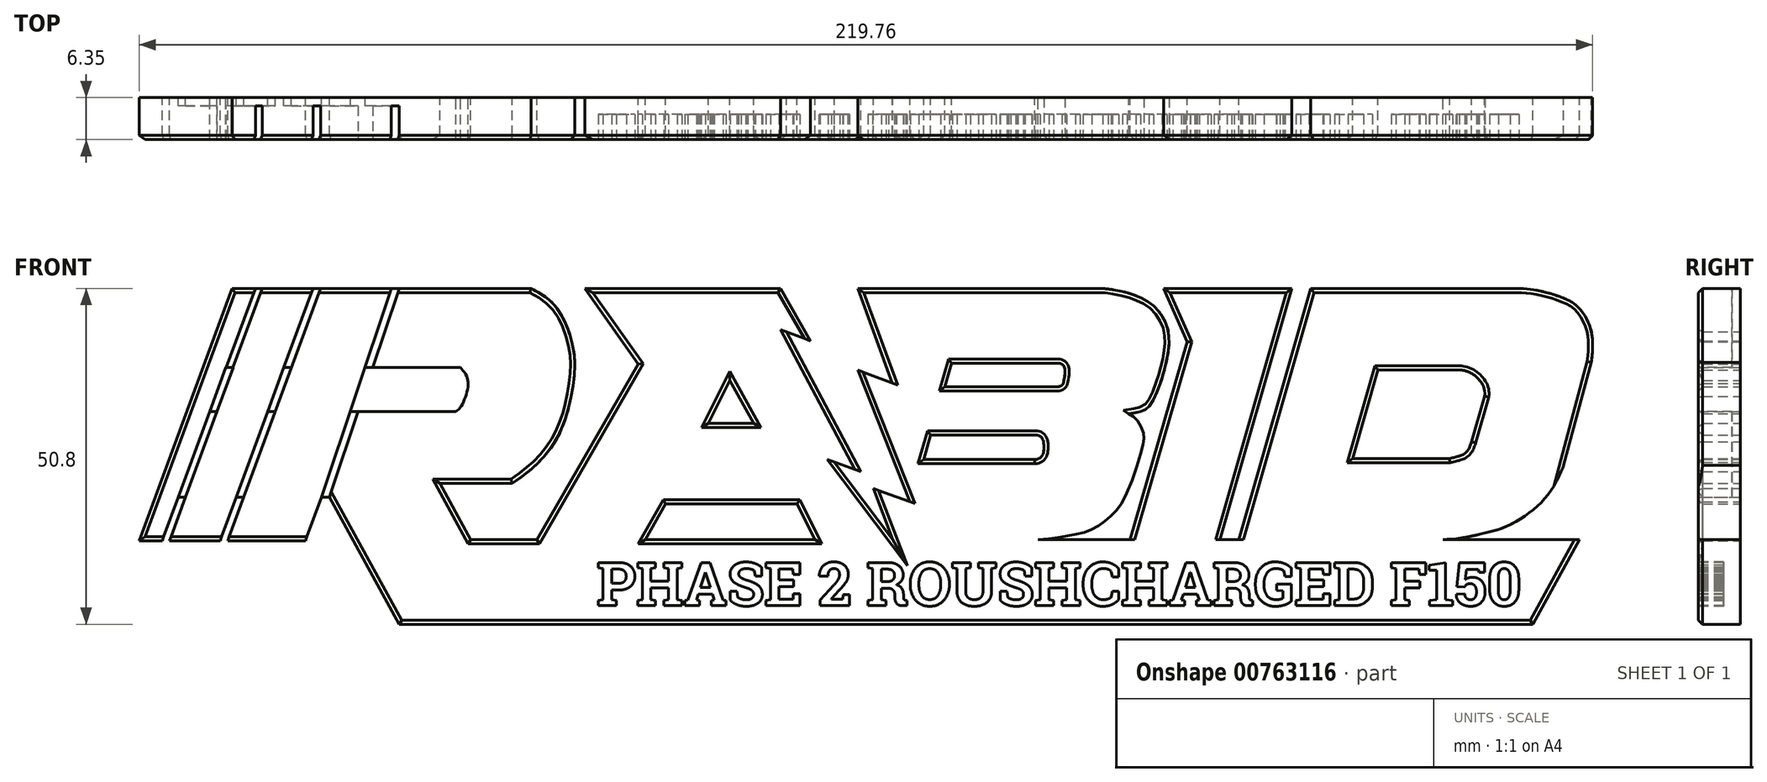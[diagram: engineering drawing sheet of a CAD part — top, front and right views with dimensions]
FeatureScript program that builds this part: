
annotation { "Feature Type Name" : "Feature", "Feature Type Description" : "" }
export const myFeature = defineFeature(function(context is Context, id is Id, definition is map)
    precondition{}
    {
        {
            var Q0;
            Q0=qCreatedBy(makeId("Front.planeOp"),FACE);
            var sketch = newSketch(context, id + "F0", { "sketchPlane" : qUnion([Q0])});
            skLineSegment(sketch, "E0", {"start": v(44.45, 18.23) * mm, "end": v(13.33, 18.23) * mm});
            skLineSegment(sketch, "E1", {"start": v(-163.82, -19.93) * mm, "end": v(-149.78, 18.23) * mm});
            skLineSegment(sketch, "E2", {"start": v(-138.67, -19.93) * mm, "end": v(-150.42, -19.93) * mm});
            skLineSegment(sketch, "E3", {"start": v(-146.28, 18.23) * mm, "end": v(-160.32, -19.93) * mm});
            skLineSegment(sketch, "E4", {"start": v(-159.23, -19.93) * mm, "end": v(-145.19, 18.23) * mm});
            skLineSegment(sketch, "E5", {"start": v(-137.53, 18.23) * mm, "end": v(-151.57, -19.93) * mm});
            skLineSegment(sketch, "E6", {"start": v(-150.42, -19.93) * mm, "end": v(-136.37, 18.23) * mm});
            skLineSegment(sketch, "E7", {"start": v(-124.63, 18.23) * mm, "end": v(-138.67, -19.93) * mm});
            skLineSegment(sketch, "E8", {"start": v(-127.97, 6.26) * mm, "end": v(-123.56, 18.23) * mm});
            skLineSegment(sketch, "E9", {"start": v(-127.97, 6.26) * mm, "end": v(-115.24, 6.26) * mm});
            skLineSegment(sketch, "E10", {"start": v(-115.92, -0.4) * mm, "end": v(-130.28, -0.4) * mm});
            skLineSegment(sketch, "E11", {"start": v(-130.28, -0.4) * mm, "end": v(-135.05, -13.36) * mm});
            skLineSegment(sketch, "E12", {"start": v(-135.05, -13.36) * mm, "end": v(-124.47, -32.57) * mm});
            skLineSegment(sketch, "E13", {"start": v(-124.47, -32.57) * mm, "end": v(-110.55, -32.57) * mm});
            skLineSegment(sketch, "E14", {"start": v(-110.55, -32.57) * mm, "end": v(-103.65, -19.74) * mm});
            skLineSegment(sketch, "E15", {"start": v(-103.65, -19.74) * mm, "end": v(-113.7, -19.74) * mm});
            skLineSegment(sketch, "E16", {"start": v(-113.7, -19.74) * mm, "end": v(-118.36, -11.28) * mm});
            skLineSegment(sketch, "E17", {"start": v(-118.36, -11.28) * mm, "end": v(-107.38, -11.28) * mm});
            skLineSegment(sketch, "E18", {"start": v(-103.65, -19.74) * mm, "end": v(-87.29, -19.74) * mm});
            skLineSegment(sketch, "E19", {"start": v(-96.42, 18.23) * mm, "end": v(-88.35, 6.81) * mm});
            skLineSegment(sketch, "E20", {"start": v(-88.35, 6.81) * mm, "end": v(-103.65, -19.74) * mm});
            skLineSegment(sketch, "E21", {"start": v(-87.29, -19.74) * mm, "end": v(-84.2, -14.4) * mm});
            skLineSegment(sketch, "E22", {"start": v(-84.2, -14.4) * mm, "end": v(-64.33, -14.4) * mm});
            skLineSegment(sketch, "E23", {"start": v(-64.33, -14.4) * mm, "end": v(-61.66, -19.74) * mm});
            skLineSegment(sketch, "E24", {"start": v(-66.84, 18.23) * mm, "end": v(-62.3, 10.3) * mm});
            skLineSegment(sketch, "E25", {"start": v(-62.3, 10.3) * mm, "end": v(-65.92, 11.65) * mm});
            skLineSegment(sketch, "E26", {"start": v(-65.92, 11.65) * mm, "end": v(-54.7, -9.5) * mm});
            skLineSegment(sketch, "E27", {"start": v(-54.7, -9.5) * mm, "end": v(-58.68, -8.06) * mm});
            skLineSegment(sketch, "E28", {"start": v(-58.68, -8.06) * mm, "end": v(-49.86, -19.74) * mm});
            skLineSegment(sketch, "E29", {"start": v(-70.89, -2.18) * mm, "end": v(-77.76, -2.18) * mm});
            skLineSegment(sketch, "E30", {"start": v(-77.76, -2.18) * mm, "end": v(-74.5, 4.32) * mm});
            skLineSegment(sketch, "E31", {"start": v(-74.5, 4.32) * mm, "end": v(-70.89, -2.18) * mm});
            skLineSegment(sketch, "E32", {"start": v(-55.14, 18.23) * mm, "end": v(-49.92, 3.87) * mm});
            skLineSegment(sketch, "E33", {"start": v(-49.92, 3.87) * mm, "end": v(-55.16, 5.86) * mm});
            skLineSegment(sketch, "E34", {"start": v(-55.16, 5.86) * mm, "end": v(-47.3, -14.02) * mm});
            skLineSegment(sketch, "E35", {"start": v(-47.3, -14.02) * mm, "end": v(-52.8, -12.04) * mm});
            skLineSegment(sketch, "E36", {"start": v(-52.8, -12.04) * mm, "end": v(-49.86, -19.74) * mm});
            skLineSegment(sketch, "E37", {"start": v(-40.97, 6.88) * mm, "end": v(-42, 3.36) * mm});
            skLineSegment(sketch, "E38", {"start": v(-45.2, -7.65) * mm, "end": v(-28.43, -7.65) * mm});
            skLineSegment(sketch, "E39", {"start": v(-44.14, -3.97) * mm, "end": v(-28.03, -3.97) * mm});
            skLineSegment(sketch, "E40", {"start": v(-40.97, 6.88) * mm, "end": v(-24.6, 6.88) * mm});
            skLineSegment(sketch, "E41", {"start": v(-42, 3.36) * mm, "end": v(-25, 3.36) * mm});
            skLineSegment(sketch, "E42", {"start": v(-8.93, 18.23) * mm, "end": v(-5.34, 10.12) * mm});
            skLineSegment(sketch, "E43", {"start": v(-5.34, 10.12) * mm, "end": v(-13.99, -19.74) * mm});
            skLineSegment(sketch, "E44", {"start": v(10.46, 18.23) * mm, "end": v(-0.4, -19.74) * mm});
            skLineSegment(sketch, "E45", {"start": v(13.33, 18.23) * mm, "end": v(2.47, -19.74) * mm});
            skLineSegment(sketch, "E46", {"start": v(35.81, 5.9) * mm, "end": v(23.48, 5.9) * mm});
            skLineSegment(sketch, "E47", {"start": v(23.48, 5.9) * mm, "end": v(19.66, -7.49) * mm});
            skLineSegment(sketch, "E48", {"start": v(19.66, -7.49) * mm, "end": v(34.3, -7.49) * mm});
            skLineSegment(sketch, "E49", {"start": v(39.6, 1.92) * mm, "end": v(37.65, -4.94) * mm});
            skFitSpline(sketch, "E50", {"points": [v(55.73, 7.05) * mm, v(55.73, 11.7) * mm, v(53.74, 15.4) * mm, v(50.9, 17) * mm, v(44.45, 18.23) * mm], "startDerivative": vector(2.3, 18.78) * mm, "endDerivative": vector(-24.45, 0) * mm});
            skLineSegment(sketch, "E51", {"start": v(55.73, 7.05) * mm, "end": v(51.56, -8.5) * mm});
            skFitSpline(sketch, "E52", {"points": [v(-14.17, -0.73) * mm, v(-12.02, -0.26) * mm, v(-10.54, 1.23) * mm, v(-8.14, 9.39) * mm, v(-8.72, 13.21) * mm, v(-10.35, 15.5) * mm, v(-13.7, 17.35) * mm, v(-18.93, 18.23) * mm], "startDerivative": vector(20.2, 3.41) * mm, "endDerivative": vector(-28.09, 0) * mm});
            skFitSpline(sketch, "E53", {"points": [v(-14.17, -0.73) * mm, v(-12.8, -1.84) * mm, v(-11.95, -3.81) * mm, v(-12.1, -5.72) * mm, v(-14.99, -13.75) * mm, v(-17.24, -16.5) * mm, v(-19.85, -18.27) * mm, v(-23.1, -19.11) * mm, v(-27.89, -19.74) * mm], "startDerivative": vector(16.43, -10.07) * mm, "endDerivative": vector(-33.98, 0) * mm});
            skFitSpline(sketch, "E54", {"points": [v(-24.6, 6.88) * mm, v(-24.2, 6.68) * mm, v(-23.87, 6.14) * mm, v(-24.05, 4.06) * mm, v(-24.29, 3.61) * mm, v(-25, 3.36) * mm], "startDerivative": vector(3.09, 0) * mm, "endDerivative": vector(-4.49, 0) * mm});
            skFitSpline(sketch, "E55", {"points": [v(-28.03, -3.97) * mm, v(-27.5, -4.2) * mm, v(-27.12, -4.85) * mm, v(-27.1, -6.65) * mm, v(-27.44, -7.25) * mm, v(-28.43, -7.65) * mm], "startDerivative": vector(3.73, 0) * mm, "endDerivative": vector(-8.7, -0.89) * mm});
            skFitSpline(sketch, "E56", {"points": [v(-104.57, 18.23) * mm, v(-101.7, 16.39) * mm, v(-99.55, 13.37) * mm, v(-98.04, 8.28) * mm, v(-98.33, 2.83) * mm, v(-99.98, -3.05) * mm, v(-103.2, -7.86) * mm, v(-107.38, -11.28) * mm], "startDerivative": vector(25.95, -13.02) * mm, "endDerivative": vector(-29.28, -21.25) * mm});
            skFitSpline(sketch, "E57", {"points": [v(35.81, 5.9) * mm, v(37.17, 5.6) * mm, v(38.23, 4.97) * mm, v(39.07, 4.03) * mm, v(39.6, 1.92) * mm], "startDerivative": vector(5.58, 0) * mm, "endDerivative": vector(-1.33, -10.82) * mm});
            skFitSpline(sketch, "E58", {"points": [v(34.3, -7.49) * mm, v(35.48, -7.2) * mm, v(36.57, -6.77) * mm, v(37.26, -5.96) * mm, v(37.65, -4.94) * mm], "startDerivative": vector(4.57, 1.01) * mm, "endDerivative": vector(1.33, 4.26) * mm});
            skLineSegment(sketch, "E59.trimOffspring", {"start": v(-146.28, 18.23) * mm, "end": v(-149.78, 18.23) * mm});
            skLineSegment(sketch, "E60.trimOffspring", {"start": v(-137.53, 18.23) * mm, "end": v(-145.19, 18.23) * mm});
            skLineSegment(sketch, "E61.trimOffspring", {"start": v(-124.63, 18.23) * mm, "end": v(-136.37, 18.23) * mm});
            skLineSegment(sketch, "E62.trimOffspring", {"start": v(-104.57, 18.23) * mm, "end": v(-123.56, 18.23) * mm});
            skLineSegment(sketch, "E63.trimOffspring", {"start": v(-151.57, -19.93) * mm, "end": v(-159.23, -19.93) * mm});
            skLineSegment(sketch, "E64.trimOffspring", {"start": v(-160.32, -19.93) * mm, "end": v(-163.82, -19.93) * mm});
            skLineSegment(sketch, "E65.trimOffspring", {"start": v(-61.66, -19.74) * mm, "end": v(-49.86, -19.74) * mm});
            skLineSegment(sketch, "E66.trimOffspring", {"start": v(-49.86, -19.74) * mm, "end": v(-27.89, -19.74) * mm});
            skLineSegment(sketch, "E67.trimOffspring", {"start": v(-66.84, 18.23) * mm, "end": v(-96.42, 18.23) * mm});
            skLineSegment(sketch, "E68.trimOffspring", {"start": v(-44.14, -3.97) * mm, "end": v(-45.2, -7.65) * mm});
            skLineSegment(sketch, "E69.trimOffspring", {"start": v(-18.93, 18.23) * mm, "end": v(-55.14, 18.23) * mm});
            skLineSegment(sketch, "E70.trimOffspring", {"start": v(-13.99, -19.74) * mm, "end": v(-0.4, -19.74) * mm});
            skLineSegment(sketch, "E71.trimOffspring", {"start": v(2.47, -19.74) * mm, "end": v(33.3, -19.74) * mm});
            skLineSegment(sketch, "E72.trimOffspring", {"start": v(10.46, 18.23) * mm, "end": v(-8.93, 18.23) * mm});
            skFitSpline(sketch, "E73", {"points": [v(51.56, -8.5) * mm, v(50.36, -11.15) * mm, v(48.41, -13.9) * mm, v(45.57, -16.27) * mm, v(42.49, -17.92) * mm, v(38.84, -18.97) * mm, v(33.3, -19.74) * mm], "startDerivative": vector(-7.47, -18.05) * mm, "endDerivative": vector(-28.9, 0) * mm});
            skFitSpline(sketch, "E74", {"points": [v(-115.24, 6.26) * mm, v(-114.2, 4.72) * mm, v(-114.26, 2.54) * mm, v(-115.24, 0.25) * mm, v(-115.92, -0.4) * mm], "startDerivative": vector(5.02, -5.67) * mm, "endDerivative": vector(-3.78, -2.78) * mm});
            skLineSegment(sketch, "E75", {"start": v(-87.29, -19.74) * mm, "end": v(-61.66, -19.74) * mm});
            skLineSegment(sketch, "E76", {"start": v(-27.89, -19.74) * mm, "end": v(-13.99, -19.74) * mm});
            skLineSegment(sketch, "E77", {"start": v(-0.4, -19.74) * mm, "end": v(2.47, -19.74) * mm});
            skLineSegment(sketch, "E78", {"start": v(27.98, -32.57) * mm, "end": v(-110.55, -32.57) * mm});
            skLineSegment(sketch, "E79", {"start": v(27.98, -32.57) * mm, "end": v(46.92, -32.57) * mm});
            skLineSegment(sketch, "E80", {"start": v(46.92, -32.57) * mm, "end": v(53.92, -19.74) * mm});
            skLineSegment(sketch, "E81", {"start": v(33.3, -19.74) * mm, "end": v(53.92, -19.74) * mm});
            skLineSegment(sketch, "E82", {"start": v(-123.56, 18.23) * mm, "end": v(-124.63, 18.23) * mm});
            skLineSegment(sketch, "E83", {"start": v(-136.37, 18.23) * mm, "end": v(-137.53, 18.23) * mm});
            skLineSegment(sketch, "E84", {"start": v(-127.97, 6.26) * mm, "end": v(-129.04, 6.26) * mm});
            skLineSegment(sketch, "E85", {"start": v(-130.28, -0.4) * mm, "end": v(-131.49, -0.4) * mm});
            skLineSegment(sketch, "E86", {"start": v(-145.19, 18.23) * mm, "end": v(-146.28, 18.23) * mm});
            skLineSegment(sketch, "E87", {"start": v(-140.78, 6.26) * mm, "end": v(-141.94, 6.26) * mm});
            skLineSegment(sketch, "E88", {"start": v(-149.6, 6.26) * mm, "end": v(-150.69, 6.26) * mm});
            skLineSegment(sketch, "E89", {"start": v(-143.23, -0.4) * mm, "end": v(-144.39, -0.4) * mm});
            skLineSegment(sketch, "E90", {"start": v(-152.05, -0.4) * mm, "end": v(-153.14, -0.4) * mm});
            skLineSegment(sketch, "E91", {"start": v(-130.28, -0.4) * mm, "end": v(-127.97, 6.26) * mm});
            skLineSegment(sketch, "E92", {"start": v(-135.05, -13.36) * mm, "end": v(-136.25, -13.36) * mm});
            skLineSegment(sketch, "E93", {"start": v(-148, -13.36) * mm, "end": v(-149.15, -13.36) * mm});
            skLineSegment(sketch, "E94", {"start": v(-156.81, -13.36) * mm, "end": v(-157.9, -13.36) * mm});
            skSolve(sketch);
        }
        {
            var Q0;
            Q0 = qSketchRegion(id + "F0", true);
            extrude(context, id + "F1", {"entities" : qUnion([Q0]), "depth" : 6.35 * mm, "offsetDistance" : 25.4 * mm});
        }
        {
            var Q0;
            {var subQ0=sQuery(id+"F0.wireOp",EDGE,"E30");var subQ1=sQuery(id+"F0.wireOp",EDGE,"E29");var subQ2=sQuery(id+"F0.wireOp",EDGE,"E27");var subQ3=sQuery(id+"F0.wireOp",EDGE,"E24");var subQ4=sQuery(id+"F0.wireOp",EDGE,"E23");var subQ5=sQuery(id+"F0.wireOp",EDGE,"E22");var subQ6=sQuery(id+"F0.wireOp",EDGE,"E21");var subQ7=sQuery(id+"F0.wireOp",EDGE,"E20");var subQ8=sQuery(id+"F0.wireOp",EDGE,"E19");var subQ9=sQuery(id+"F0.wireOp",EDGE,"E17");var subQ10=sQuery(id+"F0.wireOp",EDGE,"E16");var subQ11=sQuery(id+"F0.wireOp",EDGE,"E15");var subQ12=sQuery(id+"F0.wireOp",EDGE,"E79");var subQ13=sQuery(id+"F0.wireOp",EDGE,"E78");var subQ14=sQuery(id+"F0.wireOp",EDGE,"E13");var subQ15=sQuery(id+"F0.wireOp",EDGE,"E12");var subQ16=sQuery(id+"F0.wireOp",EDGE,"E85");var subQ17=sQuery(id+"F0.wireOp",EDGE,"E10");var subQ18=sQuery(id+"F0.wireOp",EDGE,"E84");var subQ19=sQuery(id+"F0.wireOp",EDGE,"E9");var subQ20=sQuery(id+"F0.wireOp",EDGE,"E7");var subQ21=sQuery(id+"F0.wireOp",EDGE,"E2");var subQ22=sQuery(id+"F0.wireOp",EDGE,"E92");var subQ23=sQuery(id+"F0.wireOp",EDGE,"E87");var subQ24=sQuery(id+"F0.wireOp",EDGE,"E6");var subQ25=sQuery(id+"F0.wireOp",EDGE,"E89");var subQ26=sQuery(id+"F0.wireOp",EDGE,"E93");var subQ27=sQuery(id+"F0.wireOp",EDGE,"E63.trimOffspring");var subQ28=sQuery(id+"F0.wireOp",EDGE,"E5");var subQ29=sQuery(id+"F0.wireOp",EDGE,"E88");var subQ30=sQuery(id+"F0.wireOp",EDGE,"E4");var subQ31=sQuery(id+"F0.wireOp",EDGE,"E90");var subQ32=sQuery(id+"F0.wireOp",EDGE,"E94");var subQ33=sQuery(id+"F0.wireOp",EDGE,"E64.trimOffspring");var subQ34=sQuery(id+"F0.wireOp",EDGE,"E3");var subQ35=sQuery(id+"F0.wireOp",EDGE,"E1");var subQ36=sQuery(id+"F0.wireOp",EDGE,"E0");var subQ37=sQuery(id+"F0.wireOp",EDGE,"E81");var subQ38=sQuery(id+"F0.wireOp",EDGE,"E80");var subQ39=sQuery(id+"F0.wireOp",EDGE,"E76");var subQ40=sQuery(id+"F0.wireOp",EDGE,"E75");var subQ41=sQuery(id+"F0.wireOp",EDGE,"E74");var subQ42=sQuery(id+"F0.wireOp",EDGE,"E73");var subQ43=sQuery(id+"F0.wireOp",EDGE,"E72.trimOffspring");var subQ44=sQuery(id+"F0.wireOp",EDGE,"E69.trimOffspring");var subQ45=sQuery(id+"F0.wireOp",EDGE,"E68.trimOffspring");var subQ46=sQuery(id+"F0.wireOp",EDGE,"E48");var subQ47=sQuery(id+"F0.wireOp",EDGE,"E77");var subQ48=sQuery(id+"F0.wireOp",EDGE,"E47");var subQ49=sQuery(id+"F0.wireOp",EDGE,"E45");var subQ50=sQuery(id+"F0.wireOp",EDGE,"E50");var subQ51=sQuery(id+"F0.wireOp",EDGE,"E28");var subQ52=sQuery(id+"F0.wireOp",EDGE,"E49");var subQ53=sQuery(id+"F0.wireOp",EDGE,"E46");var subQ54=sQuery(id+"F0.wireOp",EDGE,"E55");var subQ55=sQuery(id+"F0.wireOp",EDGE,"E41");var subQ56=sQuery(id+"F0.wireOp",EDGE,"E40");var subQ57=sQuery(id+"F0.wireOp",EDGE,"E32");var subQ58=sQuery(id+"F0.wireOp",EDGE,"E31");var subQ59=sQuery(id+"F0.wireOp",EDGE,"E33");var subQ60=sQuery(id+"F0.wireOp",EDGE,"E51");var subQ61=sQuery(id+"F0.wireOp",EDGE,"E44");var subQ62=sQuery(id+"F0.wireOp",EDGE,"E39");var subQ63=sQuery(id+"F0.wireOp",EDGE,"E34");var subQ64=sQuery(id+"F0.wireOp",EDGE,"E35");var subQ65=sQuery(id+"F0.wireOp",EDGE,"E36");var subQ66=sQuery(id+"F0.wireOp",EDGE,"E37");var subQ67=sQuery(id+"F0.wireOp",EDGE,"E38");var subQ68=sQuery(id+"F0.wireOp",EDGE,"E52");var subQ69=sQuery(id+"F0.wireOp",EDGE,"E53");var subQ70=sQuery(id+"F0.wireOp",EDGE,"E54");var subQ71=sQuery(id+"F0.wireOp",EDGE,"E56");var subQ72=sQuery(id+"F0.wireOp",EDGE,"E25");var subQ73=sQuery(id+"F0.wireOp",EDGE,"E57");var subQ74=sQuery(id+"F0.wireOp",EDGE,"E26");var subQ75=sQuery(id+"F0.wireOp",EDGE,"E58");var subQ76=sQuery(id+"F0.wireOp",EDGE,"E86");var subQ77=sQuery(id+"F0.wireOp",EDGE,"E83");var subQ78=sQuery(id+"F0.wireOp",EDGE,"E82");var subQ79=sQuery(id+"F0.wireOp",EDGE,"E62.trimOffspring");var subQ80=sQuery(id+"F0.wireOp",EDGE,"E61.trimOffspring");var subQ81=sQuery(id+"F0.wireOp",EDGE,"E60.trimOffspring");var subQ82=sQuery(id+"F0.wireOp",EDGE,"E59.trimOffspring");var subQ83=sQuery(id+"F0.wireOp",EDGE,"E67.trimOffspring");var subQ84=sQuery(id+"F0.wireOp",EDGE,"E42");var subQ85=sQuery(id+"F0.wireOp",EDGE,"E43");Q0=makeQuery(id+"F5.boolean.opBoolean","SPLIT",FACE,{"disambiguationData":[TD([makeQuery(id+"F1.opExtrude","SWEPT_FACE",FACE,{"disambiguationData":[OSD([subQ36])]})])],"derivedFrom":makeQuery(id+"F1.opExtrude","CAP_FACE",FACE,{"disambiguationData":[OSD([subQ36,subQ35,subQ21,subQ34,subQ30,subQ28,subQ24,subQ20,subQ19,subQ17,subQ15,subQ14,subQ11,subQ10,subQ9,subQ8,subQ7,subQ6,subQ5,subQ4,subQ3,subQ72,subQ74,subQ2,subQ51,subQ1,subQ0,subQ58,subQ57,subQ59,subQ63,subQ64,subQ65,subQ66,subQ67,subQ62,subQ56,subQ55,subQ84,subQ85,subQ61,subQ49,subQ53,subQ48,subQ46,subQ52,subQ50,subQ60,subQ68,subQ69,subQ70,subQ54,subQ71,subQ73,subQ75,subQ82,subQ81,subQ80,subQ79,subQ27,subQ33,subQ83,subQ45,subQ44,subQ43,subQ42,subQ41,subQ40,subQ39,subQ47,subQ13,subQ12,subQ38,subQ37,subQ78,subQ77,subQ18,subQ16,subQ76,subQ23,subQ29,subQ25,subQ31,subQ22,subQ26,subQ32])],"isStart":false})});}
            var sketch = newSketch(context, id + "F2", { "sketchPlane" : qUnion([Q0])});
            skLineSegment(sketch, "E95", {"start": v(-160.32, -19.93) * mm, "end": v(-159.23, -19.93) * mm});
            skLineSegment(sketch, "E96", {"start": v(-159.23, -19.93) * mm, "end": v(-145.22, 18.23) * mm});
            skLineSegment(sketch, "E97", {"start": v(-145.22, 18.23) * mm, "end": v(-146.23, 18.23) * mm});
            skLineSegment(sketch, "E98", {"start": v(-146.23, 18.23) * mm, "end": v(-160.32, -19.93) * mm});
            skLineSegment(sketch, "E99", {"start": v(-151.57, -19.93) * mm, "end": v(-150.42, -19.93) * mm});
            skLineSegment(sketch, "E100", {"start": v(-150.42, -19.93) * mm, "end": v(-136.37, 18.23) * mm});
            skLineSegment(sketch, "E101", {"start": v(-136.37, 18.23) * mm, "end": v(-137.53, 18.23) * mm});
            skLineSegment(sketch, "E102", {"start": v(-137.53, 18.23) * mm, "end": v(-151.57, -19.93) * mm});
            skPoint(sketch, "E103.endSnap0", {"position": v(-129.76, -22.96) * mm});
            skLineSegment(sketch, "E104", {"start": v(-136.25, -13.36) * mm, "end": v(-135.05, -13.36) * mm});
            skLineSegment(sketch, "E105", {"start": v(-135.05, -13.36) * mm, "end": v(-124.47, 18.23) * mm});
            skLineSegment(sketch, "E106", {"start": v(-124.47, 18.23) * mm, "end": v(-125.67, 18.23) * mm});
            skLineSegment(sketch, "E107", {"start": v(-125.67, 18.23) * mm, "end": v(-136.25, -13.36) * mm});
            skSolve(sketch);
        }
        {
            var Q0;
            Q0 = qSketchRegion(id + "F2", true);
            extrude(context, id + "F3", {"entities" : qUnion([Q0]), "operationType" : NewBodyOperationType.REMOVE, "oppositeDirection" : true, "depth" : 5.08 * mm, "offsetDistance" : 25.4 * mm});
        }
        {
            var Q0;
            Q0=makeQuery(id+"F1.opExtrude","CAP_FACE",FACE,{"disambiguationData":[OSD([sQuery(id+"F0.wireOp",EDGE,"E0"),sQuery(id+"F0.wireOp",EDGE,"E8"),sQuery(id+"F0.wireOp",EDGE,"E9"),sQuery(id+"F0.wireOp",EDGE,"E10"),sQuery(id+"F0.wireOp",EDGE,"E11"),sQuery(id+"F0.wireOp",EDGE,"E12"),sQuery(id+"F0.wireOp",EDGE,"E13"),sQuery(id+"F0.wireOp",EDGE,"E15"),sQuery(id+"F0.wireOp",EDGE,"E16"),sQuery(id+"F0.wireOp",EDGE,"E17"),sQuery(id+"F0.wireOp",EDGE,"E19"),sQuery(id+"F0.wireOp",EDGE,"E20"),sQuery(id+"F0.wireOp",EDGE,"E21"),sQuery(id+"F0.wireOp",EDGE,"E22"),sQuery(id+"F0.wireOp",EDGE,"E23"),sQuery(id+"F0.wireOp",EDGE,"E24"),sQuery(id+"F0.wireOp",EDGE,"E25"),sQuery(id+"F0.wireOp",EDGE,"E26"),sQuery(id+"F0.wireOp",EDGE,"E27"),sQuery(id+"F0.wireOp",EDGE,"E28"),sQuery(id+"F0.wireOp",EDGE,"E29"),sQuery(id+"F0.wireOp",EDGE,"E30"),sQuery(id+"F0.wireOp",EDGE,"E31"),sQuery(id+"F0.wireOp",EDGE,"E32"),sQuery(id+"F0.wireOp",EDGE,"E33"),sQuery(id+"F0.wireOp",EDGE,"E34"),sQuery(id+"F0.wireOp",EDGE,"E35"),sQuery(id+"F0.wireOp",EDGE,"E36"),sQuery(id+"F0.wireOp",EDGE,"E37"),sQuery(id+"F0.wireOp",EDGE,"E38"),sQuery(id+"F0.wireOp",EDGE,"E39"),sQuery(id+"F0.wireOp",EDGE,"E40"),sQuery(id+"F0.wireOp",EDGE,"E41"),sQuery(id+"F0.wireOp",EDGE,"E42"),sQuery(id+"F0.wireOp",EDGE,"E43"),sQuery(id+"F0.wireOp",EDGE,"E44"),sQuery(id+"F0.wireOp",EDGE,"E45"),sQuery(id+"F0.wireOp",EDGE,"E46"),sQuery(id+"F0.wireOp",EDGE,"E47"),sQuery(id+"F0.wireOp",EDGE,"E48"),sQuery(id+"F0.wireOp",EDGE,"E49"),sQuery(id+"F0.wireOp",EDGE,"E50"),sQuery(id+"F0.wireOp",EDGE,"E51"),sQuery(id+"F0.wireOp",EDGE,"E52"),sQuery(id+"F0.wireOp",EDGE,"E53"),sQuery(id+"F0.wireOp",EDGE,"E54"),sQuery(id+"F0.wireOp",EDGE,"E55"),sQuery(id+"F0.wireOp",EDGE,"E56"),sQuery(id+"F0.wireOp",EDGE,"E57"),sQuery(id+"F0.wireOp",EDGE,"E58"),sQuery(id+"F0.wireOp",EDGE,"E62.trimOffspring"),sQuery(id+"F0.wireOp",EDGE,"E67.trimOffspring"),sQuery(id+"F0.wireOp",EDGE,"E68.trimOffspring"),sQuery(id+"F0.wireOp",EDGE,"E69.trimOffspring"),sQuery(id+"F0.wireOp",EDGE,"E72.trimOffspring"),sQuery(id+"F0.wireOp",EDGE,"E73"),sQuery(id+"F0.wireOp",EDGE,"E74"),sQuery(id+"F0.wireOp",EDGE,"E75"),sQuery(id+"F0.wireOp",EDGE,"E76"),sQuery(id+"F0.wireOp",EDGE,"E77"),sQuery(id+"F0.wireOp",EDGE,"ISSC0bJT-fq30-P4vY-vGbu-V4KtggNEUtfu"),sQuery(id+"F0.wireOp",EDGE,"E78")])],"isStart":false});
            var sketch = newSketch(context, id + "F4", { "sketchPlane" : qUnion([Q0])});
            skText(sketch, "E108", { "text": "PHASE 2 ROUSHCHARGED F150", "fontName": "RobotoSlab-Bold.ttf"});
            const initialGuessF4  = {"E108": [-0.09464, -0.02976, 1, 0, 0.00662]};
            skSetInitialGuess(sketch, initialGuessF4);
            skSolve(sketch);
        }
        {
            var Q0;
            Q0 = qSketchRegion(id + "F4", true);
            extrude(context, id + "F5", {"entities" : qUnion([Q0]), "operationType" : NewBodyOperationType.REMOVE, "oppositeDirection" : true, "depth" : 3.8 * mm, "offsetDistance" : 25.4 * mm});
        }
        {
            var Q0;
            {var subQ0=sQuery(id+"F0.wireOp",EDGE,"E86");var subQ1=sQuery(id+"F0.wireOp",EDGE,"E83");var subQ2=sQuery(id+"F0.wireOp",EDGE,"E82");var subQ3=sQuery(id+"F0.wireOp",EDGE,"E62.trimOffspring");var subQ4=sQuery(id+"F0.wireOp",EDGE,"E61.trimOffspring");var subQ5=sQuery(id+"F0.wireOp",EDGE,"E60.trimOffspring");var subQ6=sQuery(id+"F0.wireOp",EDGE,"E59.trimOffspring");var subQ7=sQuery(id+"F0.wireOp",EDGE,"E1");Q0=makeQuery(id+"F3.boolean.opBoolean","SPLIT",EDGE,{"disambiguationData":[TD([makeQuery(id+"F1.opExtrude","SWEPT_FACE",FACE,{"disambiguationData":[OSD([subQ7])]})])],"derivedFrom":makeQuery(id+"F1.opExtrude","CAP_EDGE",EDGE,{"disambiguationData":[OSD([subQ6,subQ5,subQ4,subQ3,subQ2,subQ1,subQ0])],"isStart":false})});}
            var Q1;
            {var subQ0=sQuery(id+"F0.wireOp",EDGE,"E86");var subQ1=sQuery(id+"F0.wireOp",EDGE,"E83");var subQ2=sQuery(id+"F0.wireOp",EDGE,"E82");var subQ3=sQuery(id+"F0.wireOp",EDGE,"E62.trimOffspring");var subQ4=sQuery(id+"F0.wireOp",EDGE,"E61.trimOffspring");var subQ5=sQuery(id+"F0.wireOp",EDGE,"E60.trimOffspring");var subQ6=sQuery(id+"F0.wireOp",EDGE,"E59.trimOffspring");Q1=makeQuery(id+"F3.boolean.opBoolean","SPLIT",EDGE,{"disambiguationData":[TD([makeQuery(id+"F3.opExtrude","SWEPT_FACE",FACE,{"disambiguationData":[OSD([sQuery(id+"F2.wireOp",EDGE,"E96")])]})])],"derivedFrom":makeQuery(id+"F1.opExtrude","CAP_EDGE",EDGE,{"disambiguationData":[OSD([subQ6,subQ5,subQ4,subQ3,subQ2,subQ1,subQ0])],"isStart":false})});}
            var Q2;
            Q2=makeQuery(id+"F1.opExtrude","CAP_EDGE",EDGE,{"disambiguationData":[OSD([sQuery(id+"F0.wireOp",EDGE,"E2")])],"isStart":false});
            var Q3;
            Q3=makeQuery(id+"F1.opExtrude","CAP_EDGE",EDGE,{"disambiguationData":[OSD([sQuery(id+"F0.wireOp",EDGE,"E63.trimOffspring")])],"isStart":false});
            var Q4;
            Q4=makeQuery(id+"F1.opExtrude","CAP_EDGE",EDGE,{"disambiguationData":[OSD([sQuery(id+"F0.wireOp",EDGE,"E64.trimOffspring")])],"isStart":false});
            var Q5;
            Q5=makeQuery(id+"F1.opExtrude","CAP_EDGE",EDGE,{"disambiguationData":[OSD([sQuery(id+"F0.wireOp",EDGE,"E1")])],"isStart":false});
            var Q6;
            {var subQ0=sQuery(id+"F0.wireOp",EDGE,"E86");var subQ1=sQuery(id+"F0.wireOp",EDGE,"E83");var subQ2=sQuery(id+"F0.wireOp",EDGE,"E82");var subQ3=sQuery(id+"F0.wireOp",EDGE,"E62.trimOffspring");var subQ4=sQuery(id+"F0.wireOp",EDGE,"E61.trimOffspring");var subQ5=sQuery(id+"F0.wireOp",EDGE,"E60.trimOffspring");var subQ6=sQuery(id+"F0.wireOp",EDGE,"E59.trimOffspring");var subQ7=sQuery(id+"F0.wireOp",EDGE,"E56");Q6=makeQuery(id+"F3.boolean.opBoolean","SPLIT",EDGE,{"disambiguationData":[TD([makeQuery(id+"F1.opExtrude","SWEPT_FACE",FACE,{"disambiguationData":[OSD([subQ7])]})])],"derivedFrom":makeQuery(id+"F1.opExtrude","CAP_EDGE",EDGE,{"disambiguationData":[OSD([subQ6,subQ5,subQ4,subQ3,subQ2,subQ1,subQ0])],"isStart":false})});}
            var Q7;
            Q7=makeQuery(id+"F1.opExtrude","CAP_EDGE",EDGE,{"disambiguationData":[OSD([sQuery(id+"F0.wireOp",EDGE,"E56")])],"isStart":false});
            var Q8;
            Q8=makeQuery(id+"F1.opExtrude","CAP_EDGE",EDGE,{"disambiguationData":[OSD([sQuery(id+"F0.wireOp",EDGE,"E17")])],"isStart":false});
            var Q9;
            Q9=makeQuery(id+"F1.opExtrude","CAP_EDGE",EDGE,{"disambiguationData":[OSD([sQuery(id+"F0.wireOp",EDGE,"E16")])],"isStart":false});
            var Q10;
            Q10=makeQuery(id+"F1.opExtrude","CAP_EDGE",EDGE,{"disambiguationData":[OSD([sQuery(id+"F0.wireOp",EDGE,"E15")])],"isStart":false});
            var Q11;
            Q11=makeQuery(id+"F1.opExtrude","CAP_EDGE",EDGE,{"disambiguationData":[OSD([sQuery(id+"F0.wireOp",EDGE,"E20")])],"isStart":false});
            var Q12;
            Q12=makeQuery(id+"F1.opExtrude","CAP_EDGE",EDGE,{"disambiguationData":[OSD([sQuery(id+"F0.wireOp",EDGE,"E19")])],"isStart":false});
            var Q13;
            Q13=makeQuery(id+"F1.opExtrude","CAP_EDGE",EDGE,{"disambiguationData":[OSD([sQuery(id+"F0.wireOp",EDGE,"E67.trimOffspring")])],"isStart":false});
            var Q14;
            Q14=makeQuery(id+"F1.opExtrude","CAP_EDGE",EDGE,{"disambiguationData":[OSD([sQuery(id+"F0.wireOp",EDGE,"E24")])],"isStart":false});
            var Q15;
            Q15=makeQuery(id+"F1.opExtrude","CAP_EDGE",EDGE,{"disambiguationData":[OSD([sQuery(id+"F0.wireOp",EDGE,"E28")])],"isStart":false});
            var Q16;
            Q16=makeQuery(id+"F1.opExtrude","CAP_EDGE",EDGE,{"disambiguationData":[OSD([sQuery(id+"F0.wireOp",EDGE,"E36")])],"isStart":false});
            var Q17;
            Q17=makeQuery(id+"F1.opExtrude","CAP_EDGE",EDGE,{"disambiguationData":[OSD([sQuery(id+"F0.wireOp",EDGE,"E34")])],"isStart":false});
            var Q18;
            Q18=makeQuery(id+"F1.opExtrude","CAP_EDGE",EDGE,{"disambiguationData":[OSD([sQuery(id+"F0.wireOp",EDGE,"E32")])],"isStart":false});
            var Q19;
            Q19=makeQuery(id+"F1.opExtrude","CAP_EDGE",EDGE,{"disambiguationData":[OSD([sQuery(id+"F0.wireOp",EDGE,"E69.trimOffspring")])],"isStart":false});
            var Q20;
            Q20=makeQuery(id+"F1.opExtrude","CAP_EDGE",EDGE,{"disambiguationData":[OSD([sQuery(id+"F0.wireOp",EDGE,"E52")])],"isStart":false});
            var Q21;
            Q21=makeQuery(id+"F1.opExtrude","CAP_EDGE",EDGE,{"disambiguationData":[OSD([sQuery(id+"F0.wireOp",EDGE,"E43")])],"isStart":false});
            var Q22;
            Q22=makeQuery(id+"F1.opExtrude","CAP_EDGE",EDGE,{"disambiguationData":[OSD([sQuery(id+"F0.wireOp",EDGE,"E42")])],"isStart":false});
            var Q23;
            Q23=makeQuery(id+"F1.opExtrude","CAP_EDGE",EDGE,{"disambiguationData":[OSD([sQuery(id+"F0.wireOp",EDGE,"E72.trimOffspring")])],"isStart":false});
            var Q24;
            Q24=makeQuery(id+"F1.opExtrude","CAP_EDGE",EDGE,{"disambiguationData":[OSD([sQuery(id+"F0.wireOp",EDGE,"E44")])],"isStart":false});
            var Q25;
            Q25=makeQuery(id+"F1.opExtrude","CAP_EDGE",EDGE,{"disambiguationData":[OSD([sQuery(id+"F0.wireOp",EDGE,"E45")])],"isStart":false});
            var Q26;
            Q26=makeQuery(id+"F1.opExtrude","CAP_EDGE",EDGE,{"disambiguationData":[OSD([sQuery(id+"F0.wireOp",EDGE,"E0")])],"isStart":false});
            var Q27;
            Q27=makeQuery(id+"F1.opExtrude","CAP_EDGE",EDGE,{"disambiguationData":[OSD([sQuery(id+"F0.wireOp",EDGE,"E50")])],"isStart":false});
            var Q28;
            Q28=makeQuery(id+"F1.opExtrude","CAP_EDGE",EDGE,{"disambiguationData":[OSD([sQuery(id+"F0.wireOp",EDGE,"E51")])],"isStart":false});
            var Q29;
            Q29=makeQuery(id+"F1.opExtrude","CAP_EDGE",EDGE,{"disambiguationData":[OSD([sQuery(id+"F0.wireOp",EDGE,"E80")])],"isStart":false});
            var Q30;
            Q30=makeQuery(id+"F1.opExtrude","CAP_EDGE",EDGE,{"disambiguationData":[OSD([sQuery(id+"F0.wireOp",EDGE,"E13"),sQuery(id+"F0.wireOp",EDGE,"E78"),sQuery(id+"F0.wireOp",EDGE,"E79")])],"isStart":false});
            var Q31;
            Q31=makeQuery(id+"F1.opExtrude","CAP_EDGE",EDGE,{"disambiguationData":[OSD([sQuery(id+"F0.wireOp",EDGE,"E75")])],"isStart":false});
            var Q32;
            Q32=makeQuery(id+"F1.opExtrude","CAP_EDGE",EDGE,{"disambiguationData":[OSD([sQuery(id+"F0.wireOp",EDGE,"E23")])],"isStart":false});
            var Q33;
            Q33=makeQuery(id+"F1.opExtrude","CAP_EDGE",EDGE,{"disambiguationData":[OSD([sQuery(id+"F0.wireOp",EDGE,"E22")])],"isStart":false});
            var Q34;
            Q34=makeQuery(id+"F1.opExtrude","CAP_EDGE",EDGE,{"disambiguationData":[OSD([sQuery(id+"F0.wireOp",EDGE,"E21")])],"isStart":false});
            var Q35;
            Q35=makeQuery(id+"F1.opExtrude","CAP_EDGE",EDGE,{"disambiguationData":[OSD([sQuery(id+"F0.wireOp",EDGE,"E29")])],"isStart":false});
            var Q36;
            Q36=makeQuery(id+"F1.opExtrude","CAP_EDGE",EDGE,{"disambiguationData":[OSD([sQuery(id+"F0.wireOp",EDGE,"E31")])],"isStart":false});
            var Q37;
            Q37=makeQuery(id+"F1.opExtrude","CAP_EDGE",EDGE,{"disambiguationData":[OSD([sQuery(id+"F0.wireOp",EDGE,"E30")])],"isStart":false});
            var Q38;
            Q38=makeQuery(id+"F1.opExtrude","CAP_EDGE",EDGE,{"disambiguationData":[OSD([sQuery(id+"F0.wireOp",EDGE,"E38")])],"isStart":false});
            var Q39;
            Q39=makeQuery(id+"F1.opExtrude","CAP_EDGE",EDGE,{"disambiguationData":[OSD([sQuery(id+"F0.wireOp",EDGE,"E55")])],"isStart":false});
            var Q40;
            Q40=makeQuery(id+"F1.opExtrude","CAP_EDGE",EDGE,{"disambiguationData":[OSD([sQuery(id+"F0.wireOp",EDGE,"E68.trimOffspring")])],"isStart":false});
            var Q41;
            Q41=makeQuery(id+"F1.opExtrude","CAP_EDGE",EDGE,{"disambiguationData":[OSD([sQuery(id+"F0.wireOp",EDGE,"E41")])],"isStart":false});
            var Q42;
            Q42=makeQuery(id+"F1.opExtrude","CAP_EDGE",EDGE,{"disambiguationData":[OSD([sQuery(id+"F0.wireOp",EDGE,"E37")])],"isStart":false});
            var Q43;
            Q43=makeQuery(id+"F1.opExtrude","CAP_EDGE",EDGE,{"disambiguationData":[OSD([sQuery(id+"F0.wireOp",EDGE,"E26")])],"isStart":false});
            var Q44;
            Q44=makeQuery(id+"F1.opExtrude","CAP_EDGE",EDGE,{"disambiguationData":[OSD([sQuery(id+"F0.wireOp",EDGE,"E46")])],"isStart":false});
            var Q45;
            Q45=makeQuery(id+"F1.opExtrude","CAP_EDGE",EDGE,{"disambiguationData":[OSD([sQuery(id+"F0.wireOp",EDGE,"E57")])],"isStart":false});
            var Q46;
            Q46=makeQuery(id+"F1.opExtrude","CAP_EDGE",EDGE,{"disambiguationData":[OSD([sQuery(id+"F0.wireOp",EDGE,"E49")])],"isStart":false});
            var Q47;
            Q47=makeQuery(id+"F1.opExtrude","CAP_EDGE",EDGE,{"disambiguationData":[OSD([sQuery(id+"F0.wireOp",EDGE,"E58")])],"isStart":false});
            var Q48;
            Q48=makeQuery(id+"F1.opExtrude","CAP_EDGE",EDGE,{"disambiguationData":[OSD([sQuery(id+"F0.wireOp",EDGE,"E48")])],"isStart":false});
            var Q49;
            Q49=makeQuery(id+"F1.opExtrude","CAP_EDGE",EDGE,{"disambiguationData":[OSD([sQuery(id+"F0.wireOp",EDGE,"E47")])],"isStart":false});
            var Q50;
            Q50=makeQuery(id+"F1.opExtrude","CAP_EDGE",EDGE,{"disambiguationData":[OSD([sQuery(id+"F0.wireOp",EDGE,"E12")])],"isStart":false});
            var Q51;
            {var subQ3=sQuery(id+"F0.wireOp",EDGE,"E86");var subQ4=sQuery(id+"F0.wireOp",EDGE,"E83");var subQ5=sQuery(id+"F0.wireOp",EDGE,"E82");var subQ6=sQuery(id+"F0.wireOp",EDGE,"E62.trimOffspring");var subQ7=sQuery(id+"F0.wireOp",EDGE,"E61.trimOffspring");var subQ8=sQuery(id+"F0.wireOp",EDGE,"E60.trimOffspring");var subQ9=sQuery(id+"F0.wireOp",EDGE,"E59.trimOffspring");Q51=makeQuery(id+"F3.boolean.opBoolean","SPLIT",EDGE,{"disambiguationData":[TD([makeQuery(id+"F3.opExtrude","SWEPT_FACE",FACE,{"disambiguationData":[OSD([sQuery(id+"F2.wireOp",EDGE,"E100")])]})])],"derivedFrom":makeQuery(id+"F1.opExtrude","CAP_EDGE",EDGE,{"disambiguationData":[OSD([subQ9,subQ8,subQ7,subQ6,subQ5,subQ4,subQ3])],"isStart":false})});}
            chamfer(context, id + "F6", {"entities" : qUnion([Q0, Q1, Q2, Q3, Q4, Q5, Q6, Q7, Q8, Q9, Q10, Q11, Q12, Q13, Q14, Q15, Q16, Q17, Q18, Q19, Q20, Q21, Q22, Q23, Q24, Q25, Q26, Q27, Q28, Q29, Q30, Q31, Q32, Q33, Q34, Q35, Q36, Q37, Q38, Q39, Q40, Q41, Q42, Q43, Q44, Q45, Q46, Q47, Q48, Q49, Q50, Q51]), "width" : 0.64 * mm, "tangentPropagation" : true});
        }
        {
            var Q0;
            Q0=makeQuery(id+"F3.boolean.opBoolean","COPY",FACE,{"derivedFrom":makeQuery(id+"F3.opExtrude","CAP_FACE",FACE,{"disambiguationData":[OSD([sQuery(id+"F2.wireOp",EDGE,"E104"),sQuery(id+"F2.wireOp",EDGE,"E105"),sQuery(id+"F2.wireOp",EDGE,"E106"),sQuery(id+"F2.wireOp",EDGE,"E107")])],"isStart":false})});
            var sketch = newSketch(context, id + "F7", { "sketchPlane" : qUnion([Q0])});
            skLineSegment(sketch, "E109", {"start": v(-128.48, 6.26) * mm, "end": v(-129.69, 6.26) * mm});
            skLineSegment(sketch, "E110", {"start": v(-129.69, 6.26) * mm, "end": v(-131.92, -0.4) * mm});
            skLineSegment(sketch, "E111", {"start": v(-131.92, -0.4) * mm, "end": v(-130.71, -0.4) * mm});
            skLineSegment(sketch, "E112", {"start": v(-130.71, -0.4) * mm, "end": v(-128.48, 6.26) * mm});
            skSolve(sketch);
        }
        {
            var Q0;
            Q0 = qSketchRegion(id + "F7", true);
            extrude(context, id + "F8", {"entities" : qUnion([Q0]), "operationType" : NewBodyOperationType.REMOVE, "endBound" : BoundingType.THROUGH_ALL, "oppositeDirection" : true, "depth" : 25.4 * mm, "offsetDistance" : 25.4 * mm});
        }
    });
